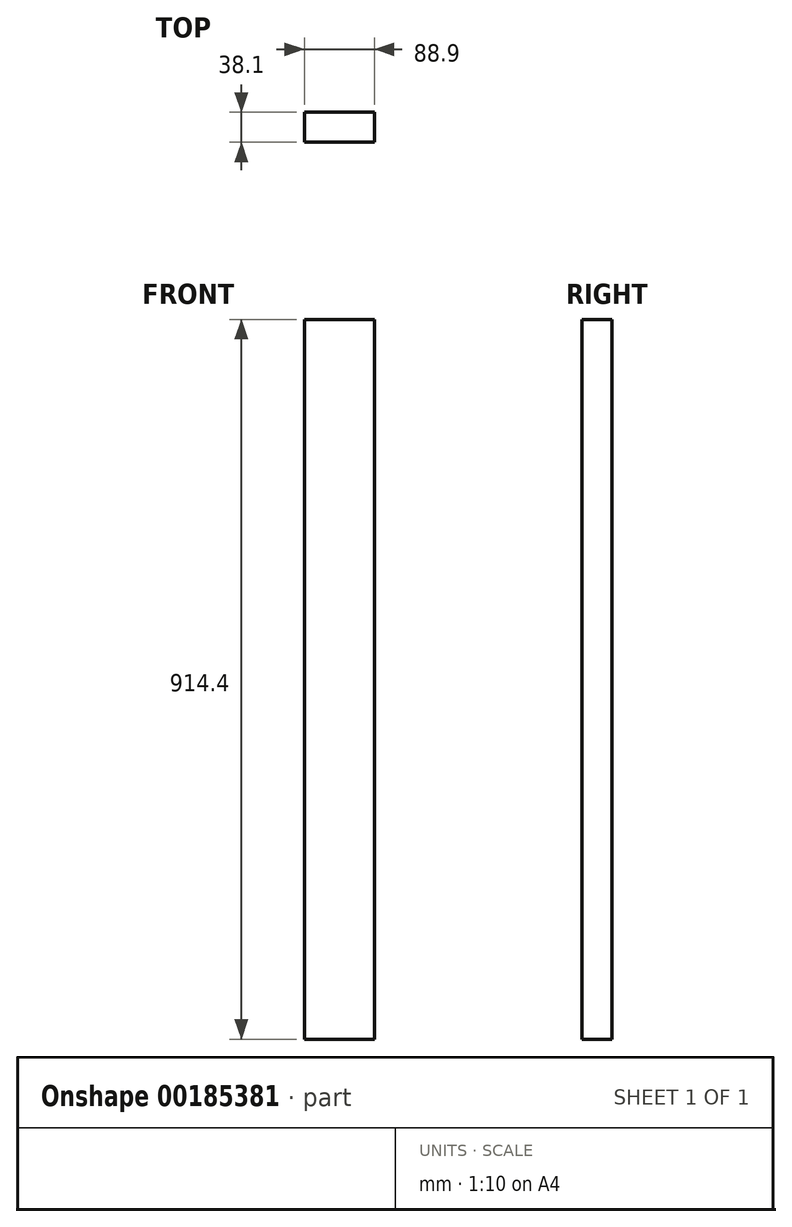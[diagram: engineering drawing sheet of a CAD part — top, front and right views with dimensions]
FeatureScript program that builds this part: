
annotation { "Feature Type Name" : "Feature", "Feature Type Description" : "" }
export const myFeature = defineFeature(function(context is Context, id is Id, definition is map)
    precondition{}
    {
        {
            var Q0;
            Q0=qCreatedBy(makeId("Top.planeOp"),FACE);
            var sketch = newSketch(context, id + "F0", { "sketchPlane" : qUnion([Q0])});
            skLineSegment(sketch, "E0.bottom", {"start": v(0, 0) * mm, "end": v(88.9, 0) * mm});
            skLineSegment(sketch, "E0.top", {"start": v(0, 38.1) * mm, "end": v(88.9, 38.1) * mm});
            skLineSegment(sketch, "E0.left", {"start": v(0, 0) * mm, "end": v(0, 38.1) * mm});
            skLineSegment(sketch, "E0.right", {"start": v(88.9, 0) * mm, "end": v(88.9, 38.1) * mm});
            skSolve(sketch);
        }
        {
            var Q0;
            Q0=makeQuery(id+"F0.imprint","IMPRINT",FACE,{"disambiguationData":[TD([[makeQuery(id+"F0.imprint","IMPRINT",EDGE,{"derivedFrom":sQuery(id+"F0.wireOp",EDGE,"E0.bottom")}),1.0]])]});
            extrude(context, id + "F1", {"entities" : qUnion([Q0]), "depth" : 914.4 * mm});
        }
    });
